# Revit family: PLASTIC SAND TRAP BASE DN100 with a high board
name_source: partatom
category: Оборудование
units: mm (PartAtom-declared; Revit-internal decimal feet)

## family parameters
Общий = Да
Основа = Грань
При загрузке вырезать с полостями = Нет
Размер круглого соединителя = Использовать диаметр
Тип детали = Нормальный
Точка расчета площади = Нет

## types (1)
- 8081
    A01 = plastic mesh : 208011
    A02 = plastic mesh : 208021
    A03 = plastic mesh ADA : 208012
    A04 = plastic mesh ADA : 208022
    A05 = plastic mesh ADA : 208032
    ADSK_Dimension_Diameter = 100 мм
    ADSK_Dimension_Height = 365 мм
    ADSK_Dimension_Lenght = 500 мм
    ADSK_Dimension_Width = 156 мм
    ADSK_Load class = C250
    ADSK_Manufacturer = Vodaland
    ADSK_Material_Name = Plastic
    ADSK_Name = Plastic sand trap Base DN100 H350 with a high board
    ADSK_Product code = 8081
    ADSK_Sealant = 11
    ADSK_Unit = pcs
    ADSK_Weight = 2.6
    Channel = Plastic sand trap Base DN100 high board : 8081
    ConnectorBack = TC : Back
    ConnectorFront = TC : Front
    ConnectorLeft = TC : Left
    ConnectorRight = TC : Right
    Dp110 = Dp : 110
    Dp160 = Dp : 160
    Dp50 = Dp : 50
    Fa1 = Choice of fastening : 6100-35
    Fa2 = Choice of fastening : 6200-35
    Fr1 = Fastening : 6100-35
    Fr2 = Fastening : 6200-35
    Fr3 = Fastening : 6800-35
    G01 = Plastic grate Base DN100 mesh : 208011
    G02 = Plastic grate Base DN100 mesh : 208021
    G03 = Plastic grate Base DN100 mesh ADA : 208012
    G04 = Plastic grate Base DN100 mesh ADA : 208022
    G05 = Plastic grate Base DN100 mesh ADA : 208032
    W1 = 160 мм
    W2 = 156 мм
    no = No : ні
    Группа модели = Linear drainage
    Отметка по умолчанию = 0 мм

## geometry (parser evidence)
native form markers: Blend x4
no freeform markers — native parametric forms only
